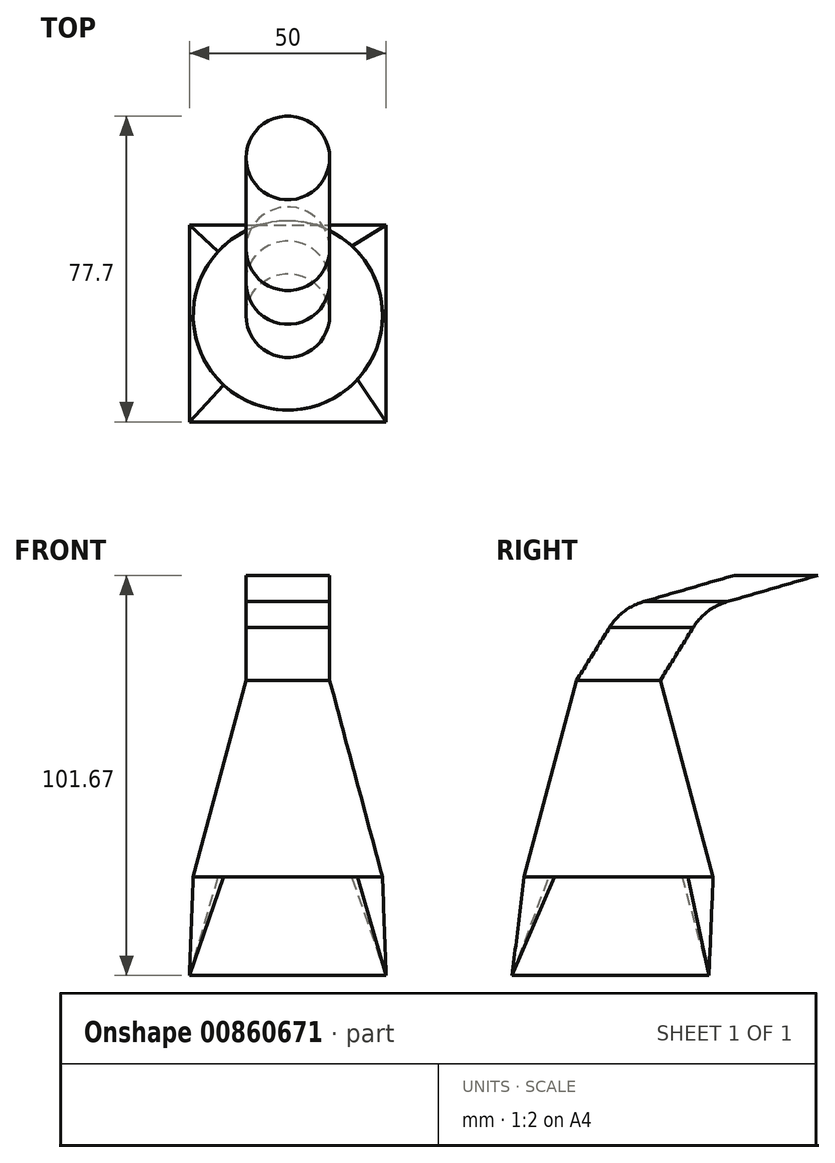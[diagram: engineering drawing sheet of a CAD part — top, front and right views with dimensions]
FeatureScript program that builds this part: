
annotation { "Feature Type Name" : "Feature", "Feature Type Description" : "" }
export const myFeature = defineFeature(function(context is Context, id is Id, definition is map)
    precondition{}
    {
        {
            var Q0;
            Q0=qCreatedBy(makeId("Top.planeOp"),FACE);
            var sketch = newSketch(context, id + "F0", { "sketchPlane" : qUnion([Q0])});
            skCircle(sketch, "E0", {"center": v(0, 0) * mm, "radius": 24.04 * mm});
            skSolve(sketch);
        }
        {
            var Q0;
            Q0 = qSketchRegion(id + "F0", true);
            extrude(context, id + "F1", {"entities" : qUnion([Q0]), "depth" : 50 * mm, "offsetDistance" : 25.4 * mm, "hasDraft" : true, "draftAngle" : 15 * degree, "draftPullDirection" : true});
        }
        {
            var Q0;
            Q0=qCreatedBy(makeId("Right.planeOp"),FACE);
            var sketch = newSketch(context, id + "F2", { "sketchPlane" : qUnion([Q0])});
            skLineSegment(sketch, "E1", {"start": v(0, 50) * mm, "end": v(8.4, 63.49) * mm});
            skLineSegment(sketch, "E2", {"start": v(16.95, 69.97) * mm, "end": v(40.05, 76.67) * mm});
            skPoint(sketch, "E3.visualSharp", {"position": v(11.43, 68.37) * mm});
            skArc(sketch, "E3.filletArc", {"start": v(16.95, 69.97) * mm, "mid": v(12.07, 67.52) * mm, "end": v(8.4, 63.49) * mm});
            skSolve(sketch);
        }
        {
            var Q0;
            Q0=makeQuery(id+"F1.opExtrude","CAP_FACE",FACE,{"disambiguationData":[OSD([sQuery(id+"F0.wireOp",EDGE,"E0")])],"isStart":false});
            var sketch = newSketch(context, id + "F3", { "sketchPlane" : qUnion([Q0])});
            skCircle(sketch, "E4.0.0", {"center": v(0, 0) * mm, "radius": 10.64 * mm});
            skSolve(sketch);
        }
        {
            var Q0;
            Q0=makeQuery(id+"F3.imprint","IMPRINT",FACE,{"disambiguationData":[TD([[makeQuery(id+"F3.imprint","IMPRINT",EDGE,{"derivedFrom":sQuery(id+"F3.wireOp",EDGE,"E4.0.0")}),1.0]])]});
            var Q1;
            Q1 = qConstructionFilter(qBodyType(qCreatedBy(id + "F2" ,EDGE), BodyType.WIRE), ConstructionObject.NO);
            sweep(context, id + "F4", {"operationType" : NewBodyOperationType.ADD, "profiles" : qUnion([Q0]), "path" : qUnion([Q1]), "keepProfileOrientation" : true});
        }
        {
            var Q0;
            Q0=qCreatedBy(makeId("Top.planeOp"),FACE);
            cPlane(context, id + "F5", {"entities" : qUnion([Q0]), "cplaneType" : CPlaneType.OFFSET, "offset" : 25 * mm, "oppositeDirection" : true, "width" : 150 * mm, "height" : 150 * mm});
        }
        {
            var Q0;
            Q0=qCreatedBy(id+"F5.planeOp",FACE);
            var sketch = newSketch(context, id + "F6", { "sketchPlane" : qUnion([Q0])});
            skLineSegment(sketch, "E5.bottom", {"start": v(-25, 22.99) * mm, "end": v(25, 22.99) * mm});
            skLineSegment(sketch, "E5.top", {"start": v(-25, -27.01) * mm, "end": v(25, -27.01) * mm});
            skLineSegment(sketch, "E5.left", {"start": v(-25, 22.99) * mm, "end": v(-25, -27.01) * mm});
            skLineSegment(sketch, "E5.right", {"start": v(25, 22.99) * mm, "end": v(25, -27.01) * mm});
            skPoint(sketch, "E5.middle", {"position": v(0, -2.01) * mm});
            skSolve(sketch);
        }
        {
            var Q0;
            Q0=makeQuery(id+"F6.imprint","IMPRINT",FACE,{"disambiguationData":[TD([[makeQuery(id+"F6.imprint","IMPRINT",EDGE,{"derivedFrom":sQuery(id+"F6.wireOp",EDGE,"E5.bottom")}),-1.0]])]});
            var Q1;
            Q1=makeQuery(id+"F1.opExtrude","CAP_FACE",FACE,{"disambiguationData":[OSD([sQuery(id+"F0.wireOp",EDGE,"E0")])],"isStart":true});
            loft(context, id + "F7", {"sheetProfilesArray" : [{ "sheetProfileEntities" : qUnion([Q0]) }, { "sheetProfileEntities" : qUnion([Q1]) }]});
        }
    });
